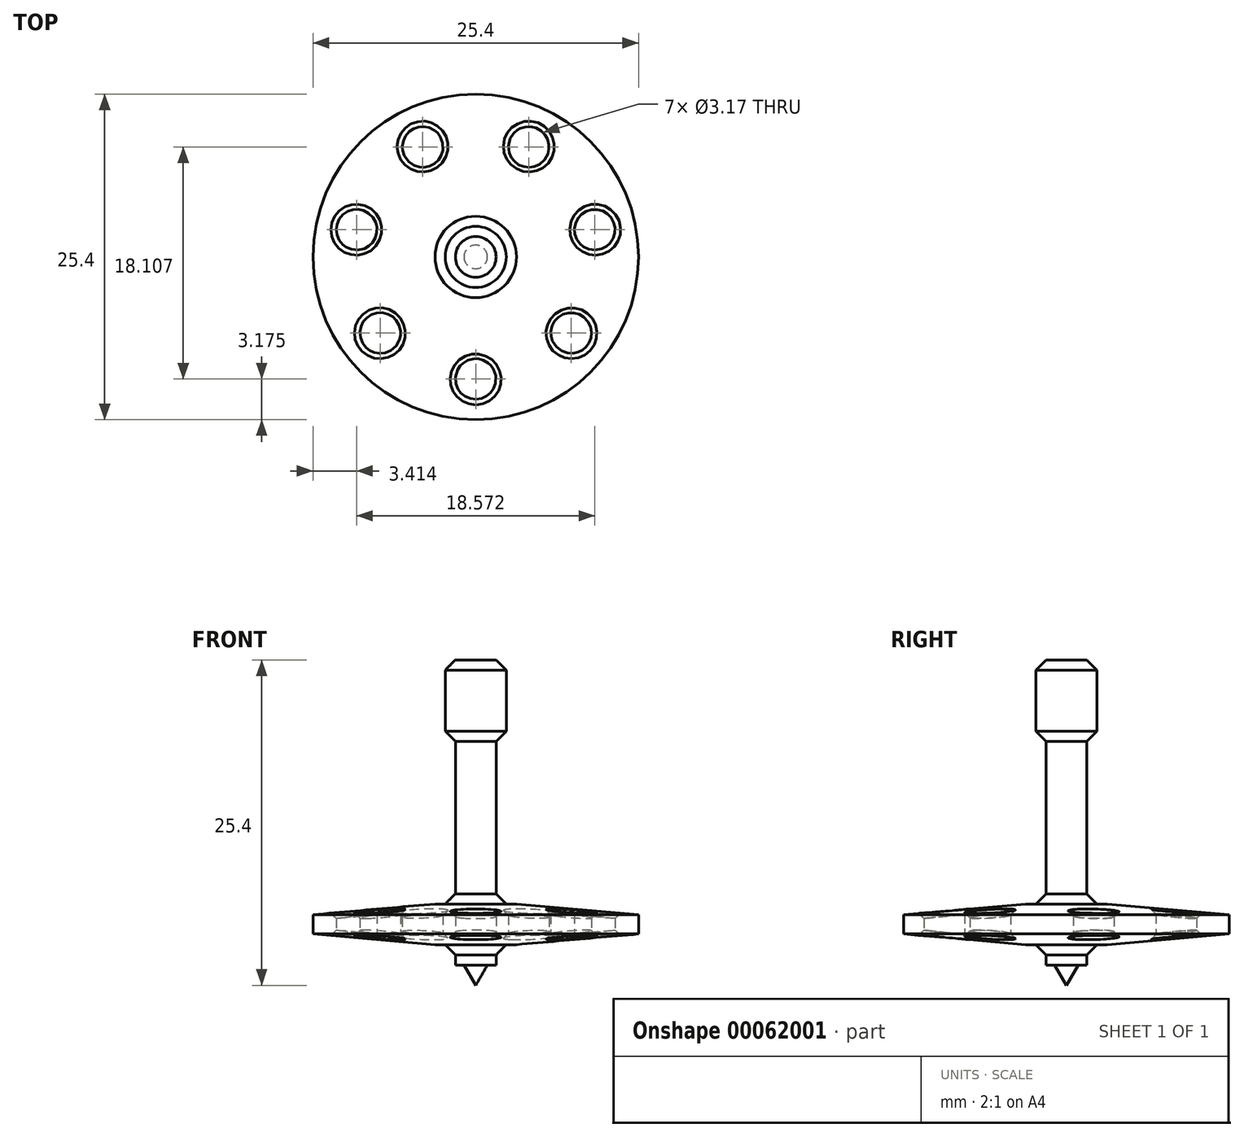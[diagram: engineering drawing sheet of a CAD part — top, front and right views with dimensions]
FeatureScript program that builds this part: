
annotation { "Feature Type Name" : "Feature", "Feature Type Description" : "" }
export const myFeature = defineFeature(function(context is Context, id is Id, definition is map)
    precondition{}
    {
        {
            var Q0;
            Q0=qCreatedBy(makeId("Front.planeOp"),FACE);
            var sketch = newSketch(context, id + "F0", { "sketchPlane" : qUnion([Q0])});
            skLineSegment(sketch, "E0", {"start": v(0, 25.4) * mm, "end": v(2.38, 25.4) * mm});
            skLineSegment(sketch, "E1", {"start": v(2.38, 25.4) * mm, "end": v(2.38, 19.05) * mm});
            skLineSegment(sketch, "E2", {"start": v(2.38, 19.05) * mm, "end": v(1.59, 19.05) * mm});
            skLineSegment(sketch, "E3", {"start": v(1.59, 19.05) * mm, "end": v(1.59, 6.35) * mm});
            skLineSegment(sketch, "E4", {"start": v(1.59, 6.35) * mm, "end": v(12.7, 6.35) * mm});
            skLineSegment(sketch, "E5", {"start": v(12.7, 6.35) * mm, "end": v(12.7, 3.18) * mm});
            skLineSegment(sketch, "E6", {"start": v(12.7, 3.18) * mm, "end": v(1.59, 3.18) * mm});
            skLineSegment(sketch, "E7", {"start": v(1.59, 3.18) * mm, "end": v(1.59, 1.59) * mm});
            skLineSegment(sketch, "E8", {"start": v(1.59, 1.59) * mm, "end": v(0.92, 1.59) * mm});
            skLineSegment(sketch, "E9", {"start": v(0.92, 1.59) * mm, "end": v(0, 0) * mm});
            skLineSegment(sketch, "E10", {"start": v(0, 0) * mm, "end": v(0, 25.4) * mm});
            skSolve(sketch);
        }
        {
            var Q0;
            Q0=makeQuery(id+"F0.imprint","IMPRINT",FACE,{"disambiguationData":[TD([[makeQuery(id+"F0.imprint","IMPRINT",EDGE,{"derivedFrom":sQuery(id+"F0.wireOp",EDGE,"E0")}),-1.0]])]});
            var Q1;
            Q1=sQuery(id+"F0.wireOp",EDGE,"E10");
            revolve(context, id + "F1", {"entities" : qUnion([Q0]), "axis" : qUnion([Q1]), "revolveType" : RevolveType.FULL});
        }
        {
            var Q0;
            Q0=makeQuery(id+"F1.opRevolve","SWEPT_EDGE",EDGE,{"disambiguationData":[OSD([sQuery(id+"F0.wireOp",EDGE,"E0"),sQuery(id+"F0.wireOp",EDGE,"E1")])]});
            var Q1;
            Q1=makeQuery(id+"F1.opRevolve","SWEPT_EDGE",EDGE,{"disambiguationData":[OSD([sQuery(id+"F0.wireOp",EDGE,"E1"),sQuery(id+"F0.wireOp",EDGE,"E2")])]});
            var Q2;
            Q2=makeQuery(id+"F1.opRevolve","SWEPT_EDGE",EDGE,{"disambiguationData":[OSD([sQuery(id+"F0.wireOp",EDGE,"E3"),sQuery(id+"F0.wireOp",EDGE,"E4")])]});
            var Q3;
            Q3=makeQuery(id+"F1.opRevolve","SWEPT_EDGE",EDGE,{"disambiguationData":[OSD([sQuery(id+"F0.wireOp",EDGE,"E6"),sQuery(id+"F0.wireOp",EDGE,"E7")])]});
            chamfer(context, id + "F2", {"entities" : qUnion([Q0, Q1, Q2, Q3]), "width" : 0.8 * mm, "tangentPropagation" : true});
        }
        {
            var Q0;
            Q0=makeQuery(id+"F1.opRevolve","SWEPT_EDGE",EDGE,{"disambiguationData":[OSD([sQuery(id+"F0.wireOp",EDGE,"E4"),sQuery(id+"F0.wireOp",EDGE,"E5")])]});
            var Q1;
            Q1=makeQuery(id+"F1.opRevolve","SWEPT_EDGE",EDGE,{"disambiguationData":[OSD([sQuery(id+"F0.wireOp",EDGE,"E5"),sQuery(id+"F0.wireOp",EDGE,"E6")])]});
            chamfer(context, id + "F3", {"entities" : qUnion([Q0, Q1]), "chamferType" : ChamferType.OFFSET_ANGLE, "width" : 9.52 * mm, "oppositeDirection" : true, "angle" : 5 * degree, "tangentPropagation" : true});
        }
        {
            var Q0;
            Q0=makeQuery(id+"F1.opRevolve","SWEPT_FACE",FACE,{"disambiguationData":[OSD([sQuery(id+"F0.wireOp",EDGE,"E6")])]});
            var sketch = newSketch(context, id + "F5", { "sketchPlane" : qUnion([Q0])});
            skCircle(sketch, "E11", {"center": v(0, 9.53) * mm, "radius": 1.59 * mm});
            skCircle(sketch, "E12", {"center": v(7.45, 5.94) * mm, "radius": 1.59 * mm});
            skCircle(sketch, "E13", {"center": v(4.13, -8.58) * mm, "radius": 1.59 * mm});
            skCircle(sketch, "E14", {"center": v(-4.13, -8.58) * mm, "radius": 1.59 * mm});
            skCircle(sketch, "E15", {"center": v(-9.29, -2.12) * mm, "radius": 1.59 * mm});
            skCircle(sketch, "E16", {"center": v(0, 0) * mm, "radius": 9.53 * mm, "construction": true});
            skLineSegment(sketch, "E17", {"start": v(0, 0) * mm, "end": v(0, 9.53) * mm, "construction": true});
            skLineSegment(sketch, "E18", {"start": v(0, 0) * mm, "end": v(7.45, 5.94) * mm, "construction": true});
            skLineSegment(sketch, "E19", {"start": v(0, 0) * mm, "end": v(4.13, -8.58) * mm, "construction": true});
            skLineSegment(sketch, "E20", {"start": v(0, 0) * mm, "end": v(-4.13, -8.58) * mm, "construction": true});
            skLineSegment(sketch, "E21", {"start": v(0, 0) * mm, "end": v(-9.29, -2.12) * mm, "construction": true});
            skLineSegment(sketch, "E22", {"start": v(0, 0) * mm, "end": v(-7.45, 5.94) * mm, "construction": true});
            skLineSegment(sketch, "E23", {"start": v(0, 0) * mm, "end": v(9.29, -2.12) * mm, "construction": true});
            skCircle(sketch, "E24", {"center": v(-7.45, 5.94) * mm, "radius": 1.59 * mm});
            skCircle(sketch, "E25", {"center": v(9.29, -2.12) * mm, "radius": 1.59 * mm});
            skSolve(sketch);
        }
        {
            var Q0;
            Q0 = qSketchRegion(id + "F5", true);
            var Q1;
            Q1=makeQuery(id+"F1.opRevolve","SWEPT_FACE",FACE,{"disambiguationData":[OSD([sQuery(id+"F0.wireOp",EDGE,"E4")])]});
            extrude(context, id + "F6", {"entities" : qUnion([Q0]), "operationType" : NewBodyOperationType.REMOVE, "endBound" : BoundingType.UP_TO_SURFACE, "oppositeDirection" : true, "endBoundEntityFace" : qUnion([Q1]), "depth" : 25.4 * mm});
        }
        {
            var Q0;
            Q0=makeQuery(id+"F6.boolean.opBoolean","INTERSECT",EDGE,{"derivedFrom":[makeQuery(id+"F3.opChamfer","BLEND_FACE",FACE,{"disambiguationData":[OSD([sQuery(id+"F0.wireOp",EDGE,"E4"),sQuery(id+"F0.wireOp",EDGE,"E5")])]}),makeQuery(id+"F6.opExtrude","SWEPT_FACE",FACE,{"disambiguationData":[OSD([sQuery(id+"F5.wireOp",EDGE,"E15")])]})]});
            var Q1;
            Q1=makeQuery(id+"F6.boolean.opBoolean","INTERSECT",EDGE,{"derivedFrom":[makeQuery(id+"F3.opChamfer","BLEND_FACE",FACE,{"disambiguationData":[OSD([sQuery(id+"F0.wireOp",EDGE,"E4"),sQuery(id+"F0.wireOp",EDGE,"E5")])]}),makeQuery(id+"F6.opExtrude","SWEPT_FACE",FACE,{"disambiguationData":[OSD([sQuery(id+"F5.wireOp",EDGE,"E14")])]})]});
            var Q2;
            Q2=makeQuery(id+"F6.boolean.opBoolean","INTERSECT",EDGE,{"derivedFrom":[makeQuery(id+"F3.opChamfer","BLEND_FACE",FACE,{"disambiguationData":[OSD([sQuery(id+"F0.wireOp",EDGE,"E4"),sQuery(id+"F0.wireOp",EDGE,"E5")])]}),makeQuery(id+"F6.opExtrude","SWEPT_FACE",FACE,{"disambiguationData":[OSD([sQuery(id+"F5.wireOp",EDGE,"E13")])]})]});
            var Q3;
            Q3=makeQuery(id+"F6.boolean.opBoolean","INTERSECT",EDGE,{"derivedFrom":[makeQuery(id+"F3.opChamfer","BLEND_FACE",FACE,{"disambiguationData":[OSD([sQuery(id+"F0.wireOp",EDGE,"E4"),sQuery(id+"F0.wireOp",EDGE,"E5")])]}),makeQuery(id+"F6.opExtrude","SWEPT_FACE",FACE,{"disambiguationData":[OSD([sQuery(id+"F5.wireOp",EDGE,"E25")])]})]});
            var Q4;
            Q4=makeQuery(id+"F6.boolean.opBoolean","INTERSECT",EDGE,{"derivedFrom":[makeQuery(id+"F3.opChamfer","BLEND_FACE",FACE,{"disambiguationData":[OSD([sQuery(id+"F0.wireOp",EDGE,"E4"),sQuery(id+"F0.wireOp",EDGE,"E5")])]}),makeQuery(id+"F6.opExtrude","SWEPT_FACE",FACE,{"disambiguationData":[OSD([sQuery(id+"F5.wireOp",EDGE,"E12")])]})]});
            var Q5;
            Q5=makeQuery(id+"F6.boolean.opBoolean","INTERSECT",EDGE,{"derivedFrom":[makeQuery(id+"F3.opChamfer","BLEND_FACE",FACE,{"disambiguationData":[OSD([sQuery(id+"F0.wireOp",EDGE,"E4"),sQuery(id+"F0.wireOp",EDGE,"E5")])]}),makeQuery(id+"F6.opExtrude","SWEPT_FACE",FACE,{"disambiguationData":[OSD([sQuery(id+"F5.wireOp",EDGE,"E11")])]})]});
            var Q6;
            Q6=makeQuery(id+"F6.boolean.opBoolean","INTERSECT",EDGE,{"derivedFrom":[makeQuery(id+"F3.opChamfer","BLEND_FACE",FACE,{"disambiguationData":[OSD([sQuery(id+"F0.wireOp",EDGE,"E4"),sQuery(id+"F0.wireOp",EDGE,"E5")])]}),makeQuery(id+"F6.opExtrude","SWEPT_FACE",FACE,{"disambiguationData":[OSD([sQuery(id+"F5.wireOp",EDGE,"E24")])]})]});
            var Q7;
            Q7=makeQuery(id+"F6.boolean.opBoolean","INTERSECT",EDGE,{"derivedFrom":[makeQuery(id+"F3.opChamfer","BLEND_FACE",FACE,{"disambiguationData":[OSD([sQuery(id+"F0.wireOp",EDGE,"E5"),sQuery(id+"F0.wireOp",EDGE,"E6")])]}),makeQuery(id+"F6.opExtrude","SWEPT_FACE",FACE,{"disambiguationData":[OSD([sQuery(id+"F5.wireOp",EDGE,"E24")])]})]});
            var Q8;
            Q8=makeQuery(id+"F6.boolean.opBoolean","INTERSECT",EDGE,{"derivedFrom":[makeQuery(id+"F3.opChamfer","BLEND_FACE",FACE,{"disambiguationData":[OSD([sQuery(id+"F0.wireOp",EDGE,"E5"),sQuery(id+"F0.wireOp",EDGE,"E6")])]}),makeQuery(id+"F6.opExtrude","SWEPT_FACE",FACE,{"disambiguationData":[OSD([sQuery(id+"F5.wireOp",EDGE,"E15")])]})]});
            var Q9;
            Q9=makeQuery(id+"F6.boolean.opBoolean","INTERSECT",EDGE,{"derivedFrom":[makeQuery(id+"F3.opChamfer","BLEND_FACE",FACE,{"disambiguationData":[OSD([sQuery(id+"F0.wireOp",EDGE,"E5"),sQuery(id+"F0.wireOp",EDGE,"E6")])]}),makeQuery(id+"F6.opExtrude","SWEPT_FACE",FACE,{"disambiguationData":[OSD([sQuery(id+"F5.wireOp",EDGE,"E14")])]})]});
            var Q10;
            Q10=makeQuery(id+"F6.boolean.opBoolean","INTERSECT",EDGE,{"derivedFrom":[makeQuery(id+"F3.opChamfer","BLEND_FACE",FACE,{"disambiguationData":[OSD([sQuery(id+"F0.wireOp",EDGE,"E5"),sQuery(id+"F0.wireOp",EDGE,"E6")])]}),makeQuery(id+"F6.opExtrude","SWEPT_FACE",FACE,{"disambiguationData":[OSD([sQuery(id+"F5.wireOp",EDGE,"E13")])]})]});
            var Q11;
            Q11=makeQuery(id+"F6.boolean.opBoolean","INTERSECT",EDGE,{"derivedFrom":[makeQuery(id+"F3.opChamfer","BLEND_FACE",FACE,{"disambiguationData":[OSD([sQuery(id+"F0.wireOp",EDGE,"E5"),sQuery(id+"F0.wireOp",EDGE,"E6")])]}),makeQuery(id+"F6.opExtrude","SWEPT_FACE",FACE,{"disambiguationData":[OSD([sQuery(id+"F5.wireOp",EDGE,"E25")])]})]});
            var Q12;
            Q12=makeQuery(id+"F6.boolean.opBoolean","INTERSECT",EDGE,{"derivedFrom":[makeQuery(id+"F3.opChamfer","BLEND_FACE",FACE,{"disambiguationData":[OSD([sQuery(id+"F0.wireOp",EDGE,"E5"),sQuery(id+"F0.wireOp",EDGE,"E6")])]}),makeQuery(id+"F6.opExtrude","SWEPT_FACE",FACE,{"disambiguationData":[OSD([sQuery(id+"F5.wireOp",EDGE,"E12")])]})]});
            var Q13;
            Q13=makeQuery(id+"F6.boolean.opBoolean","INTERSECT",EDGE,{"derivedFrom":[makeQuery(id+"F3.opChamfer","BLEND_FACE",FACE,{"disambiguationData":[OSD([sQuery(id+"F0.wireOp",EDGE,"E5"),sQuery(id+"F0.wireOp",EDGE,"E6")])]}),makeQuery(id+"F6.opExtrude","SWEPT_FACE",FACE,{"disambiguationData":[OSD([sQuery(id+"F5.wireOp",EDGE,"E11")])]})]});
            chamfer(context, id + "F7", {"entities" : qUnion([Q0, Q1, Q2, Q3, Q4, Q5, Q6, Q7, Q8, Q9, Q10, Q11, Q12, Q13]), "width" : 0.4 * mm, "tangentPropagation" : true});
        }
    });
